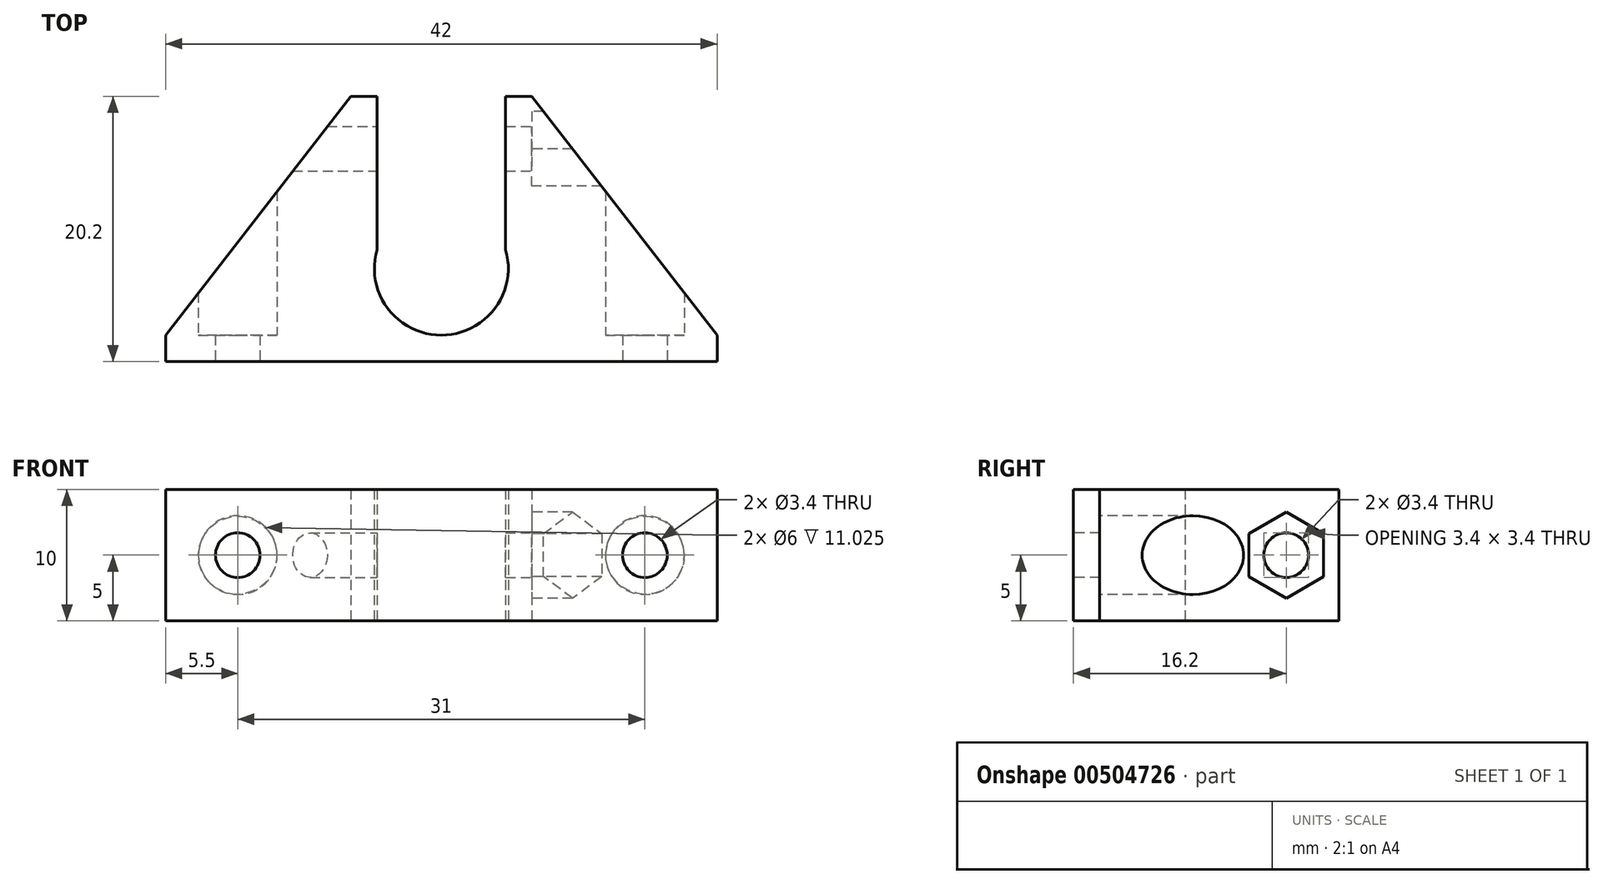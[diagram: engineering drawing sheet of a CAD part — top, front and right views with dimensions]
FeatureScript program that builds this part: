
annotation { "Feature Type Name" : "Feature", "Feature Type Description" : "" }
export const myFeature = defineFeature(function(context is Context, id is Id, definition is map)
    precondition{}
    {
        {
            var Q0;
            Q0=qCreatedBy(makeId("Top.planeOp"),FACE);
            var sketch = newSketch(context, id + "F0", { "sketchPlane" : qUnion([Q0])});
            skLineSegment(sketch, "E0", {"start": v(-21, 0) * mm, "end": v(21, 0) * mm});
            skLineSegment(sketch, "E1", {"start": v(-21, 0) * mm, "end": v(-21, 2) * mm});
            skLineSegment(sketch, "E2", {"start": v(-21, 2) * mm, "end": v(-6.9, 20.2) * mm});
            skLineSegment(sketch, "E3", {"start": v(-6.9, 20.2) * mm, "end": v(-4.9, 20.2) * mm});
            skLineSegment(sketch, "E4", {"start": v(6.9, 20.2) * mm, "end": v(21, 2) * mm});
            skLineSegment(sketch, "E5", {"start": v(21, 2) * mm, "end": v(21, 0) * mm});
            skArc(sketch, "E6", {"start": v(-4.9, 8.51) * mm, "mid": v(0, 2) * mm, "end": v(4.9, 8.51) * mm});
            skPoint(sketch, "E7", {"position": v(0, 20.2) * mm});
            skPoint(sketch, "E8", {"position": v(0, 2) * mm});
            skPoint(sketch, "E9", {"position": v(0, 12.2) * mm});
            skLineSegment(sketch, "E10", {"start": v(0, 20.2) * mm, "end": v(0, 12.2) * mm, "construction": true});
            skLineSegment(sketch, "E11", {"start": v(-10, 16.2) * mm, "end": v(10, 16.2) * mm, "construction": true});
            skPoint(sketch, "E12", {"position": v(0, 16.2) * mm});
            skLineSegment(sketch, "E13", {"start": v(-15.5, 0) * mm, "end": v(15.5, 0) * mm, "construction": true});
            skPoint(sketch, "E14", {"position": v(0, 0) * mm});
            skLineSegment(sketch, "E15", {"start": v(-15.5, 0) * mm, "end": v(-15.5, 16.2) * mm, "construction": true});
            skLineSegment(sketch, "E16", {"start": v(15.5, 0) * mm, "end": v(15.5, 16.2) * mm, "construction": true});
            skLineSegment(sketch, "E17", {"start": v(4.9, 8.51) * mm, "end": v(4.9, 20.2) * mm});
            skLineSegment(sketch, "E18", {"start": v(-4.9, 8.51) * mm, "end": v(-4.9, 20.2) * mm});
            skPoint(sketch, "E19", {"position": v(5.1, 7.1) * mm});
            skLineSegment(sketch, "E20.trimOffspring", {"start": v(4.9, 20.2) * mm, "end": v(6.9, 20.2) * mm});
            skSolve(sketch);
        }
        {
            var Q0;
            Q0=qSketchRegion(id+"F0",true);
            extrude(context, id + "F1", {"entities" : qUnion([Q0]), "endBound" : BoundingType.SYMMETRIC, "depth" : 10 * mm});
        }
        {
            var Q0;
            Q0=qCreatedBy(makeId("Front.planeOp"),FACE);
            var sketch = newSketch(context, id + "F2", { "sketchPlane" : qUnion([Q0])});
            skCircle(sketch, "E21", {"center": v(-15.5, 0) * mm, "radius": 1.7 * mm});
            skCircle(sketch, "E22", {"center": v(15.5, 0) * mm, "radius": 1.7 * mm});
            skSolve(sketch);
        }
        {
            var Q0;
            Q0=qSketchRegion(id+"F2",true);
            extrude(context, id + "F3", {"entities" : qUnion([Q0]), "operationType" : NewBodyOperationType.REMOVE, "endBound" : BoundingType.THROUGH_ALL, "oppositeDirection" : true, "depth" : 25 * mm});
        }
        {
            var Q0;
            Q0=qCreatedBy(makeId("Front.planeOp"),FACE);
            var Q1;
            Q1=sQuery(id+"F0.wireOp",VERTEX,"E2.start");
            cPlane(context, id + "F4", {"entities" : qUnion([Q0, Q1]), "cplaneType" : CPlaneType.PLANE_POINT, "offset" : 25 * mm, "width" : 150 * mm, "height" : 150 * mm});
        }
        {
            var Q0;
            Q0=qCreatedBy(id+"F4.planeOp",FACE);
            var sketch = newSketch(context, id + "F5", { "sketchPlane" : qUnion([Q0])});
            skCircle(sketch, "E23", {"center": v(-15.5, 0) * mm, "radius": 3 * mm});
            skCircle(sketch, "E24", {"center": v(15.5, 0) * mm, "radius": 3 * mm});
            skSolve(sketch);
        }
        {
            var Q0;
            Q0=qSketchRegion(id+"F5",true);
            extrude(context, id + "F6", {"entities" : qUnion([Q0]), "operationType" : NewBodyOperationType.REMOVE, "endBound" : BoundingType.THROUGH_ALL, "oppositeDirection" : true, "depth" : 25 * mm});
        }
        {
            var Q0;
            Q0=qCreatedBy(makeId("Right.planeOp"),FACE);
            var sketch = newSketch(context, id + "F7", { "sketchPlane" : qUnion([Q0])});
            skCircle(sketch, "E25", {"center": v(16.2, 0) * mm, "radius": 1.7 * mm});
            skSolve(sketch);
        }
        {
            var Q0;
            Q0=qCreatedBy(makeId("Right.planeOp"),FACE);
            var Q1;
            Q1=sQuery(id+"F0.wireOp",VERTEX,"E4.start");
            cPlane(context, id + "F8", {"entities" : qUnion([Q0, Q1]), "cplaneType" : CPlaneType.PLANE_POINT, "offset" : 25 * mm, "width" : 150 * mm, "height" : 150 * mm});
        }
        {
            var Q0;
            Q0=qSketchRegion(id+"F7",true);
            extrude(context, id + "F9", {"entities" : qUnion([Q0]), "operationType" : NewBodyOperationType.REMOVE, "endBound" : BoundingType.THROUGH_ALL, "oppositeDirection" : true, "depth" : 25 * mm, "hasSecondDirection" : true, "secondDirectionBound" : SecondDirectionBoundingType.THROUGH_ALL, "secondDirectionOppositeDirection" : false, "secondDirectionDepth" : 25 * mm});
        }
        {
            var Q0;
            Q0=qCreatedBy(id+"F8.planeOp",FACE);
            var sketch = newSketch(context, id + "F10", { "sketchPlane" : qUnion([Q0])});
            skCircle(sketch, "E26.cCircle", {"center": v(16.2, 0) * mm, "radius": 2.85 * mm, "construction": true});
            skLineSegment(sketch, "E26.0", {"start": v(19.05, -1.65) * mm, "end": v(16.2, -3.3) * mm});
            skLineSegment(sketch, "E26.1", {"start": v(16.2, -3.3) * mm, "end": v(13.35, -1.65) * mm});
            skLineSegment(sketch, "E26.2", {"start": v(13.35, -1.65) * mm, "end": v(13.35, 1.65) * mm});
            skLineSegment(sketch, "E26.3", {"start": v(13.35, 1.65) * mm, "end": v(16.2, 3.3) * mm});
            skLineSegment(sketch, "E26.4", {"start": v(16.2, 3.3) * mm, "end": v(19.05, 1.65) * mm});
            skLineSegment(sketch, "E26.5", {"start": v(19.05, 1.65) * mm, "end": v(19.05, -1.65) * mm});
            skPoint(sketch, "E26.0.midPoint", {"position": v(17.62, -2.47) * mm});
            skSolve(sketch);
        }
        {
            var Q0;
            Q0=qSketchRegion(id+"F10",true);
            extrude(context, id + "F11", {"entities" : qUnion([Q0]), "operationType" : NewBodyOperationType.REMOVE, "endBound" : BoundingType.THROUGH_ALL, "depth" : 25 * mm});
        }
    });
